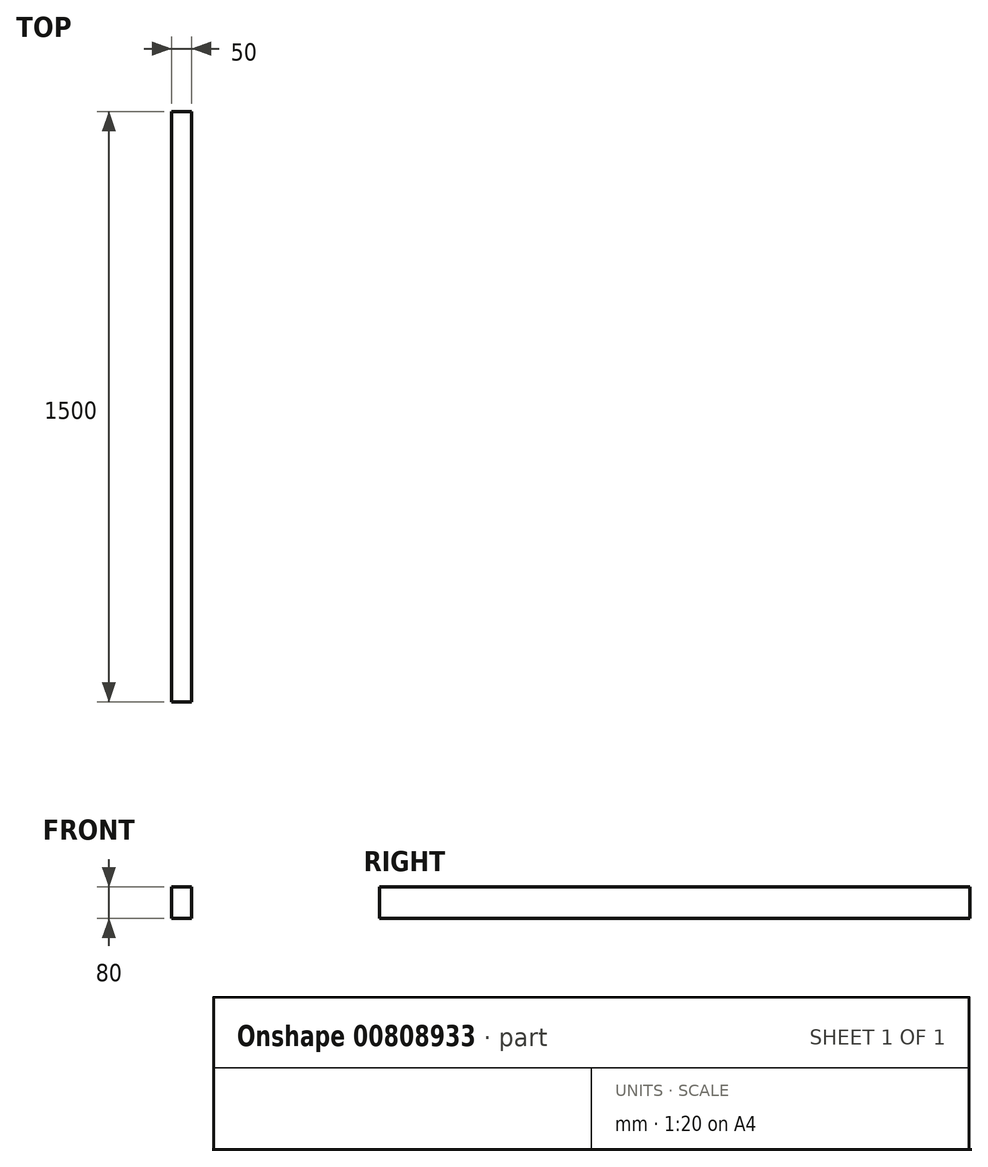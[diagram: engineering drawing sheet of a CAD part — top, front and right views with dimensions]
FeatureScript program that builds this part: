
annotation { "Feature Type Name" : "Feature", "Feature Type Description" : "" }
export const myFeature = defineFeature(function(context is Context, id is Id, definition is map)
    precondition{}
    {
        {
            var Q0;
            Q0=qCreatedBy(makeId("Top.planeOp"),FACE);
            var sketch = newSketch(context, id + "F0", { "sketchPlane" : qUnion([Q0])});
            skLineSegment(sketch, "E0.bottom", {"start": v(0, 0) * mm, "end": v(50, 0) * mm});
            skLineSegment(sketch, "E0.top", {"start": v(0, 1500) * mm, "end": v(50, 1500) * mm});
            skLineSegment(sketch, "E0.left", {"start": v(0, 0) * mm, "end": v(0, 1500) * mm});
            skLineSegment(sketch, "E0.right", {"start": v(50, 0) * mm, "end": v(50, 1500) * mm});
            skSolve(sketch);
        }
        {
            var Q0;
            Q0=makeQuery(id+"F0.imprint","IMPRINT",FACE,{"disambiguationData":[TD([[makeQuery(id+"F0.imprint","IMPRINT",EDGE,{"derivedFrom":sQuery(id+"F0.wireOp",EDGE,"E0.bottom")}),1.0]])]});
            extrude(context, id + "F1", {"entities" : qUnion([Q0]), "depth" : 80 * mm, "offsetDistance" : 25 * mm});
        }
    });
